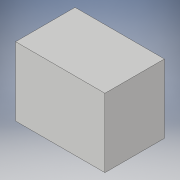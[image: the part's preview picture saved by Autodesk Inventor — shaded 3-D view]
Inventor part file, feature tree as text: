
AUTODESK INVENTOR PART (.ipt)
format: ipt  version: 2019 (Build 230136000, 136)  size: 84,992 bytes
history: native  units: mm
features: extrude x1, sketch x1
ambient origin geometry x8: Origin, YZ Plane, XZ Plane, XY Plane, X Axis, Y Axis, Z Axis, Center Point
bodies: Solid1 (feature_tree)
feature tree (2):
  extrude  "Extrusion1"  Depth=200.0mm
  sketch  "Sketch1"  dims[d0=260.0mm d1=200.0mm d2=173.0mm d3=0.0mm]
